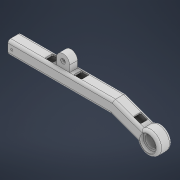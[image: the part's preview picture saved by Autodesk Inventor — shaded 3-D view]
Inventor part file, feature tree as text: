
AUTODESK INVENTOR PART (.ipt)
format: ipt  version: 2021 (Build 250183000, 183)  size: 538,112 bytes
history: native  units: mm
features: extrude x11, sketch x9, fillet x2, shell x1
ambient origin geometry x8: Origin, YZ Plane, XZ Plane, XY Plane, X Axis, Y Axis, Z Axis, Center Point
bodies: Volumenkörper1 (feature_tree)
feature tree (23):
  sketch  "Skizze1"  dims[d5=20.0mm d56=0.0mm]
  sketch  "Skizze4"  dims[d57=0.0mm d58=60.0mm]
  extrude  "Extrusion1"  TaperAngle=0.0deg  [1 undecoded]
  sketch  "Skizze13"  dims[d129=12.0mm d130=0.0mm d133=3.2mm]
  extrude  "Extrusion13"  Depth=60.0mm
  extrude  "Extrusion14"  Depth=10.0mm TaperAngle=0.0deg
  shell  "Wandung2"  Thickness=10.0mm
  extrude  "Extrusion11"  Depth=12.0mm
  extrude  "Extrusion12"  Depth=10.0mm TaperAngle=0.0deg
  extrude  "Extrusion15"  Depth=3.490659mm
  extrude  "Extrusion16"  Depth=10.0mm
  extrude  "Extrusion17"  Depth=10.0mm
  extrude  "Extrusion18"  Depth=2.0mm
  fillet  "Rundung7"  Radius=34.0mm
  extrude  "Extrusion19"  Depth=2.0mm TaperAngle=0.0deg
  extrude  "Extrusion20"  Depth=2.0mm TaperAngle=0.0deg
  fillet  "Rundung8"  Radius=2.6mm
  sketch  "Skizze12"  dims[d74=20.0mm d75=20.0mm d78=10.0mm d79=20.0mm d80=0.0mm d116=10.0mm]
  sketch  "Skizze14"  dims[d135=6.0mm d136=10.0mm d137=0.0mm]
  sketch  "Skizze15"  dims[d138=160.0mm d140=3.490659mm]
  sketch  "Skizze16"  dims[d141=10.0mm d142=110.0mm]
  sketch  "Skizze17"  dims[d143=50.0mm d144=10.0mm]
  sketch  "Skizze18"  dims[d147=10.0mm d148=24.3mm d149=34.0mm d150=20.0mm d151=0.0mm d152=20.0mm d153=0.0mm d154=2.6mm d155=4.0mm d157=18.0mm d158=10.0mm d159=0.0mm d160=10.0mm d161=10.0mm d162=20.0mm d163=6.0mm d164=0.0mm d165=7.0mm d166=10.0mm d167=10.0mm d168=10.0mm d169=3.0mm d170=0.0mm d171=3.2mm d172=10.0mm d173=10.0mm d174=3.0mm d175=0.0mm d176=12.0mm d177=12.0mm d178=6.0mm d179=12.0mm d180=12.0mm d181=6.0mm d182=3.0mm d183=0.0mm d184=12.0mm d185=12.0mm d186=6.0mm d187=3.0mm d188=0.0mm d189=2.0mm d81=0.5mm d82=0.872665mm d83=0.5mm d84=0.872665mm]
note: 1 required parameter value undecoded (feature->parameter linkage not recoverable at this tier; creation-order binding heuristic only, values carry confidence <= 0.55)
